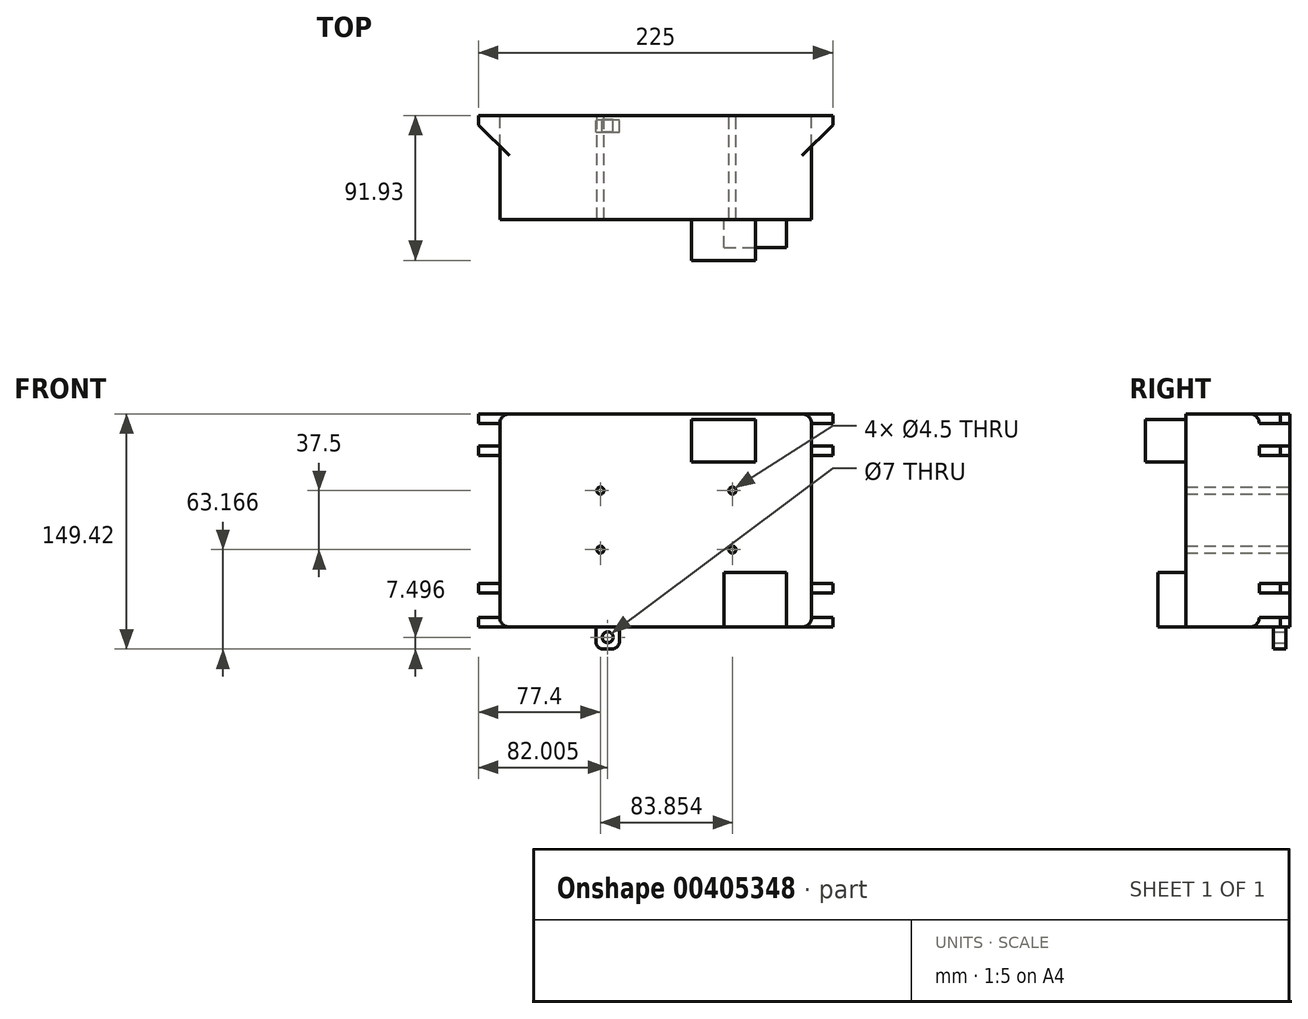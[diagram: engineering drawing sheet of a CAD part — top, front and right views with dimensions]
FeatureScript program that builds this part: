
annotation { "Feature Type Name" : "Feature", "Feature Type Description" : "" }
export const myFeature = defineFeature(function(context is Context, id is Id, definition is map)
    precondition{}
    {
        {
            var Q0;
            Q0=qCreatedBy(makeId("Front.planeOp"),FACE);
            var sketch = newSketch(context, id + "F0", { "sketchPlane" : qUnion([Q0])});
            skPoint(sketch, "E0", {"position": v(-106.19, 61.28) * mm});
            skPoint(sketch, "E1", {"position": v(91.81, -74.14) * mm});
            skPoint(sketch, "E2", {"position": v(91.81, 61.28) * mm});
            skPoint(sketch, "E3", {"position": v(-106.19, -74.14) * mm});
            skPoint(sketch, "E4", {"position": v(102.31, -60.3) * mm});
            skPoint(sketch, "E5", {"position": v(102.31, 48.09) * mm});
            skPoint(sketch, "E6", {"position": v(-116.69, 48.09) * mm});
            skPoint(sketch, "E7", {"position": v(-116.69, -60.3) * mm});
            skLineSegment(sketch, "E8.bottom", {"start": v(-100.19, 61.28) * mm, "end": v(85.81, 61.28) * mm});
            skLineSegment(sketch, "E8.top", {"start": v(-100.19, -74.14) * mm, "end": v(85.81, -74.14) * mm});
            skLineSegment(sketch, "E8.left", {"start": v(-106.19, 55.28) * mm, "end": v(-106.19, -68.14) * mm});
            skLineSegment(sketch, "E8.right", {"start": v(91.81, 55.28) * mm, "end": v(91.81, -68.14) * mm});
            skLineSegment(sketch, "E9.bottom", {"start": v(85.81, 61.28) * mm, "end": v(106.81, 61.28) * mm});
            skLineSegment(sketch, "E9.top", {"start": v(91.81, 34.9) * mm, "end": v(106.81, 34.9) * mm});
            skLineSegment(sketch, "E9.left", {"start": v(91.81, 55.28) * mm, "end": v(91.81, 34.9) * mm});
            skLineSegment(sketch, "E9.right", {"start": v(112.81, 55.28) * mm, "end": v(112.81, 40.9) * mm});
            skLineSegment(sketch, "E10.bottom", {"start": v(85.81, -74.14) * mm, "end": v(106.81, -74.14) * mm});
            skLineSegment(sketch, "E10.top", {"start": v(91.81, -46.46) * mm, "end": v(106.81, -46.46) * mm});
            skLineSegment(sketch, "E10.left", {"start": v(91.81, -68.14) * mm, "end": v(91.81, -46.46) * mm});
            skLineSegment(sketch, "E10.right", {"start": v(112.81, -68.14) * mm, "end": v(112.81, -52.46) * mm});
            skLineSegment(sketch, "E11.bottom", {"start": v(-100.19, -74.14) * mm, "end": v(-121.19, -74.14) * mm});
            skLineSegment(sketch, "E11.top", {"start": v(-106.19, -46.46) * mm, "end": v(-121.19, -46.46) * mm});
            skLineSegment(sketch, "E11.left", {"start": v(-106.19, -68.14) * mm, "end": v(-106.19, -46.46) * mm});
            skLineSegment(sketch, "E11.right", {"start": v(-127.19, -68.14) * mm, "end": v(-127.19, -52.46) * mm});
            skLineSegment(sketch, "E12.bottom", {"start": v(-106.19, 61.28) * mm, "end": v(-121.19, 61.28) * mm});
            skLineSegment(sketch, "E12.top", {"start": v(-106.19, 34.9) * mm, "end": v(-121.19, 34.9) * mm});
            skLineSegment(sketch, "E12.left", {"start": v(-106.19, 55.28) * mm, "end": v(-106.19, 34.9) * mm});
            skLineSegment(sketch, "E12.right", {"start": v(-127.19, 55.28) * mm, "end": v(-127.19, 40.9) * mm});
            skPoint(sketch, "E13.visualSharp", {"position": v(-127.19, 61.28) * mm});
            skArc(sketch, "E13.filletArc", {"start": v(-121.19, 61.28) * mm, "mid": v(-125.43, 59.52) * mm, "end": v(-127.19, 55.28) * mm});
            skPoint(sketch, "E14.visualSharp", {"position": v(-127.19, -74.14) * mm});
            skArc(sketch, "E14.filletArc", {"start": v(-127.19, -68.14) * mm, "mid": v(-125.43, -72.39) * mm, "end": v(-121.19, -74.14) * mm});
            skPoint(sketch, "E15.visualSharp", {"position": v(-127.19, -46.46) * mm});
            skArc(sketch, "E15.filletArc", {"start": v(-121.19, -46.46) * mm, "mid": v(-125.43, -48.22) * mm, "end": v(-127.19, -52.46) * mm});
            skPoint(sketch, "E16.visualSharp", {"position": v(112.81, -46.46) * mm});
            skArc(sketch, "E16.filletArc", {"start": v(112.81, -52.46) * mm, "mid": v(111.06, -48.22) * mm, "end": v(106.81, -46.46) * mm});
            skPoint(sketch, "E17.visualSharp", {"position": v(112.81, -74.14) * mm});
            skArc(sketch, "E17.filletArc", {"start": v(106.81, -74.14) * mm, "mid": v(111.06, -72.39) * mm, "end": v(112.81, -68.14) * mm});
            skPoint(sketch, "E18.visualSharp", {"position": v(112.81, 34.9) * mm});
            skArc(sketch, "E18.filletArc", {"start": v(106.81, 34.9) * mm, "mid": v(111.06, 36.66) * mm, "end": v(112.81, 40.9) * mm});
            skPoint(sketch, "E19.visualSharp", {"position": v(112.81, 61.28) * mm});
            skArc(sketch, "E19.filletArc", {"start": v(112.81, 55.28) * mm, "mid": v(111.06, 59.52) * mm, "end": v(106.81, 61.28) * mm});
            skPoint(sketch, "E20.visualSharp", {"position": v(-127.19, 34.9) * mm});
            skArc(sketch, "E20.filletArc", {"start": v(-127.19, 40.9) * mm, "mid": v(-125.43, 36.66) * mm, "end": v(-121.19, 34.9) * mm});
            skCircle(sketch, "E21", {"center": v(-116.69, -60.3) * mm, "radius": 3.75 * mm});
            skCircle(sketch, "E22", {"center": v(-116.69, 48.09) * mm, "radius": 3.75 * mm});
            skCircle(sketch, "E23", {"center": v(102.31, 48.09) * mm, "radius": 3.75 * mm});
            skCircle(sketch, "E24", {"center": v(102.31, -60.3) * mm, "radius": 3.75 * mm});
            skPoint(sketch, "E25", {"position": v(274.58, -41.3) * mm});
            skPoint(sketch, "E26", {"position": v(292.5, -41.3) * mm});
            skLineSegment(sketch, "E27.0", {"start": v(-112.19, 34.9) * mm, "end": v(-112.19, -46.46) * mm});
            skLineSegment(sketch, "E28.0", {"start": v(97.81, 34.9) * mm, "end": v(97.81, -46.46) * mm});
            skArc(sketch, "E29.filletArc", {"start": v(-100.19, 61.28) * mm, "mid": v(-104.43, 59.52) * mm, "end": v(-106.19, 55.28) * mm});
            skArc(sketch, "E30.filletArc", {"start": v(91.81, 55.28) * mm, "mid": v(90.06, 59.52) * mm, "end": v(85.81, 61.28) * mm});
            skArc(sketch, "E31.filletArc", {"start": v(85.81, -74.14) * mm, "mid": v(90.06, -72.39) * mm, "end": v(91.81, -68.14) * mm});
            skArc(sketch, "E32.filletArc", {"start": v(-106.19, -68.14) * mm, "mid": v(-104.43, -72.39) * mm, "end": v(-100.19, -74.14) * mm});
            skLineSegment(sketch, "E33", {"start": v(-106.19, 61.28) * mm, "end": v(-100.19, 61.28) * mm});
            skLineSegment(sketch, "E34.0", {"start": v(-119.69, 61.28) * mm, "end": v(-119.69, 55.28) * mm});
            skLineSegment(sketch, "E35.0", {"start": v(-106.19, 55.28) * mm, "end": v(-119.69, 55.28) * mm});
            skLineSegment(sketch, "E36.0", {"start": v(-106.19, 40.9) * mm, "end": v(-119.69, 40.9) * mm});
            skLineSegment(sketch, "E37.trimOffspring", {"start": v(-119.69, 40.9) * mm, "end": v(-119.69, 34.9) * mm});
            skLineSegment(sketch, "E38.0", {"start": v(85.81, 55.28) * mm, "end": v(105.31, 55.28) * mm});
            skLineSegment(sketch, "E39.0", {"start": v(91.81, 40.9) * mm, "end": v(105.31, 40.9) * mm});
            skLineSegment(sketch, "E40.0", {"start": v(91.81, -52.46) * mm, "end": v(105.31, -52.46) * mm});
            skLineSegment(sketch, "E41.0", {"start": v(85.81, -68.14) * mm, "end": v(105.31, -68.14) * mm});
            skLineSegment(sketch, "E42.0", {"start": v(-100.19, -68.14) * mm, "end": v(-119.69, -68.14) * mm});
            skLineSegment(sketch, "E43.0", {"start": v(-106.19, -52.46) * mm, "end": v(-119.69, -52.46) * mm});
            skLineSegment(sketch, "E44.0", {"start": v(-119.69, -74.14) * mm, "end": v(-119.69, -68.14) * mm});
            skLineSegment(sketch, "E45.0", {"start": v(105.31, 61.28) * mm, "end": v(105.31, 55.28) * mm});
            skLineSegment(sketch, "E46.trimOffspring", {"start": v(105.31, 40.9) * mm, "end": v(105.31, 34.9) * mm});
            skLineSegment(sketch, "E47.trimOffspring", {"start": v(105.31, -46.46) * mm, "end": v(105.31, -52.46) * mm});
            skLineSegment(sketch, "E48.trimOffspring", {"start": v(105.31, -68.14) * mm, "end": v(105.31, -74.14) * mm});
            skLineSegment(sketch, "E49.trimOffspring", {"start": v(-119.69, -52.46) * mm, "end": v(-119.69, -46.46) * mm});
            skLineSegment(sketch, "E50.0", {"start": v(-40.19, -88.14) * mm, "end": v(-35.19, -88.14) * mm});
            skLineSegment(sketch, "E51.0", {"start": v(-30.19, -74.14) * mm, "end": v(-30.19, -83.14) * mm});
            skLineSegment(sketch, "E52.0", {"start": v(-45.19, -74.14) * mm, "end": v(-45.19, -83.14) * mm});
            skLineSegment(sketch, "E53", {"start": v(-37.69, -88.14) * mm, "end": v(-37.69, -74.14) * mm, "construction": true});
            skLineSegment(sketch, "E54.0", {"start": v(-45.19, -80.64) * mm, "end": v(-30.19, -80.64) * mm, "construction": true});
            skCircle(sketch, "E55", {"center": v(-37.69, -80.64) * mm, "radius": 3.5 * mm});
            skPoint(sketch, "E56.visualSharp", {"position": v(-45.19, -88.14) * mm});
            skArc(sketch, "E56.filletArc", {"start": v(-45.19, -83.14) * mm, "mid": v(-43.72, -86.68) * mm, "end": v(-40.19, -88.14) * mm});
            skPoint(sketch, "E57.visualSharp", {"position": v(-30.19, -88.14) * mm});
            skArc(sketch, "E57.filletArc", {"start": v(-35.19, -88.14) * mm, "mid": v(-31.65, -86.68) * mm, "end": v(-30.19, -83.14) * mm});
            skLineSegment(sketch, "E58.0", {"start": v(-100.19, 12.53) * mm, "end": v(85.81, 12.53) * mm, "construction": true});
            skLineSegment(sketch, "E59.0", {"start": v(41.56, 55.28) * mm, "end": v(41.56, -68.14) * mm, "construction": true});
            skLineSegment(sketch, "E60.0", {"start": v(-100.19, -24.97) * mm, "end": v(85.81, -24.97) * mm, "construction": true});
            skLineSegment(sketch, "E61.0", {"start": v(-42.29, 55.28) * mm, "end": v(-42.29, -68.14) * mm, "construction": true});
            skCircle(sketch, "E62", {"center": v(-42.29, 12.53) * mm, "radius": 2.25 * mm});
            skCircle(sketch, "E63", {"center": v(41.56, 12.53) * mm, "radius": 2.25 * mm});
            skCircle(sketch, "E64", {"center": v(-42.29, -24.97) * mm, "radius": 2.25 * mm});
            skCircle(sketch, "E65", {"center": v(41.56, -24.97) * mm, "radius": 2.25 * mm});
            skSolve(sketch);
        }
        {
            var Q0;
            Q0=makeQuery(id+"F0.imprint","IMPRINT",FACE,{"disambiguationData":[TD([[makeQuery(id+"F0.imprint","IMPRINT",EDGE,{"derivedFrom":sQuery(id+"F0.wireOp",EDGE,"E8.bottom")}),-1.0]])]});
            extrude(context, id + "F1", {"entities" : qUnion([Q0]), "depth" : 66 * mm});
        }
        {
            var Q0;
            Q0=makeQuery(id+"F0.imprint","IMPRINT",FACE,{"disambiguationData":[TD([[makeQuery(id+"F0.imprint","IMPRINT",EDGE,{"derivedFrom":sQuery(id+"F0.wireOp",EDGE,"E12.right")}),1.0]])]});
            var Q1;
            Q1=makeQuery(id+"F0.imprint","IMPRINT",FACE,{"disambiguationData":[TD([[makeQuery(id+"F0.imprint","IMPRINT",EDGE,{"derivedFrom":sQuery(id+"F0.wireOp",EDGE,"E9.right")}),-1.0]])]});
            var Q2;
            Q2=makeQuery(id+"F0.imprint","IMPRINT",FACE,{"disambiguationData":[TD([[makeQuery(id+"F0.imprint","IMPRINT",EDGE,{"derivedFrom":sQuery(id+"F0.wireOp",EDGE,"E10.right")}),1.0]])]});
            var Q3;
            Q3=makeQuery(id+"F0.imprint","IMPRINT",FACE,{"disambiguationData":[TD([[makeQuery(id+"F0.imprint","IMPRINT",EDGE,{"derivedFrom":sQuery(id+"F0.wireOp",EDGE,"E11.right")}),-1.0]])]});
            var Q4;
            Q4=makeQuery(id+"F0.imprint","IMPRINT",FACE,{"disambiguationData":[TD([[makeQuery(id+"F0.imprint","IMPRINT",EDGE,{"derivedFrom":sQuery(id+"F0.wireOp",EDGE,"E29.filletArc")}),-1.0]])]});
            var Q5;
            {var subQ0=sQuery(id+"F0.wireOp",EDGE,"E36.0");Q5=makeQuery(id+"F0.imprint","IMPRINT",FACE,{"disambiguationData":[TD([[makeQuery(id+"F0.imprint","IMPRINT",EDGE,{"derivedFrom":subQ0}),1.0]])]});}
            var Q6;
            {var subQ0=sQuery(id+"F0.wireOp",EDGE,"E43.0");Q6=makeQuery(id+"F0.imprint","IMPRINT",FACE,{"disambiguationData":[TD([[makeQuery(id+"F0.imprint","IMPRINT",EDGE,{"derivedFrom":subQ0}),-1.0]])]});}
            var Q7;
            {var subQ0=sQuery(id+"F0.wireOp",EDGE,"E32.filletArc");Q7=makeQuery(id+"F0.imprint","IMPRINT",FACE,{"disambiguationData":[TD([[makeQuery(id+"F0.imprint","IMPRINT",EDGE,{"derivedFrom":subQ0}),-1.0]])]});}
            var Q8;
            {var subQ0=sQuery(id+"F0.wireOp",EDGE,"E31.filletArc");Q8=makeQuery(id+"F0.imprint","IMPRINT",FACE,{"disambiguationData":[TD([[makeQuery(id+"F0.imprint","IMPRINT",EDGE,{"derivedFrom":subQ0}),-1.0]])]});}
            var Q9;
            {var subQ0=sQuery(id+"F0.wireOp",EDGE,"E40.0");Q9=makeQuery(id+"F0.imprint","IMPRINT",FACE,{"disambiguationData":[TD([[makeQuery(id+"F0.imprint","IMPRINT",EDGE,{"derivedFrom":subQ0}),1.0]])]});}
            var Q10;
            {var subQ0=sQuery(id+"F0.wireOp",EDGE,"E39.0");Q10=makeQuery(id+"F0.imprint","IMPRINT",FACE,{"disambiguationData":[TD([[makeQuery(id+"F0.imprint","IMPRINT",EDGE,{"derivedFrom":subQ0}),-1.0]])]});}
            var Q11;
            {var subQ0=sQuery(id+"F0.wireOp",EDGE,"E30.filletArc");Q11=makeQuery(id+"F0.imprint","IMPRINT",FACE,{"disambiguationData":[TD([[makeQuery(id+"F0.imprint","IMPRINT",EDGE,{"derivedFrom":subQ0}),-1.0]])]});}
            extrude(context, id + "F2", {"entities" : qUnion([Q0, Q1, Q2, Q3, Q4, Q5, Q6, Q7, Q8, Q9, Q10, Q11]), "operationType" : NewBodyOperationType.ADD, "depth" : 6 * mm});
        }
        {
            var Q0;
            Q0=makeQuery(id+"F7.boolean.opBoolean","MERGE",FACE,{"derivedFrom":[makeQuery(id+"F2.boolean.opBoolean","MERGE",FACE,{"derivedFrom":[makeQuery(id+"F1.opExtrude","SWEPT_FACE",FACE,{"disambiguationData":[OSD([sQuery(id+"F0.wireOp",EDGE,"E8.top")])]}),makeQuery(id+"F2.opExtrude","SWEPT_FACE",FACE,{"disambiguationData":[OSD([sQuery(id+"F0.wireOp",EDGE,"E10.bottom")])]}),makeQuery(id+"F2.opExtrude","SWEPT_FACE",FACE,{"disambiguationData":[OSD([sQuery(id+"F0.wireOp",EDGE,"E11.bottom")])]})]}),makeQuery(id+"F7.opExtrude","SWEPT_FACE",FACE,{"disambiguationData":[OSD([sQuery(id+"F5.wireOp",EDGE,"E81.top")])]})]});
            var sketch = newSketch(context, id + "F3", { "sketchPlane" : qUnion([Q0])});
            skPoint(sketch, "E66.0", {"position": v(-119.69, 0) * mm});
            skLineSegment(sketch, "E67", {"start": v(-119.69, 0) * mm, "end": v(-119.69, 6) * mm, "construction": true});
            skLineSegment(sketch, "E68", {"start": v(-119.69, 6) * mm, "end": v(-100.19, 25.5) * mm});
            skPoint(sketch, "E69.0", {"position": v(105.31, 0) * mm});
            skLineSegment(sketch, "E70", {"start": v(105.31, 0) * mm, "end": v(105.31, 6) * mm, "construction": true});
            skLineSegment(sketch, "E71", {"start": v(105.31, 6) * mm, "end": v(85.81, 25.5) * mm});
            skSolve(sketch);
        }
        {
            var Q0;
            Q0=sQuery(id+"F3.wireOp",EDGE,"E68");
            var Q1;
            Q1=sQuery(id+"F3.wireOp",EDGE,"E71");
            extrude(context, id + "F4", {"bodyType" : ExtendedToolBodyType.SURFACE, "surfaceEntities" : qUnion([Q0, Q1]), "oppositeDirection" : true, "depth" : 140 * mm});
        }
        {
            var Q0;
            Q0=makeQuery(id+"F1.opExtrude","CAP_FACE",FACE,{"disambiguationData":[OSD([sQuery(id+"F0.wireOp",EDGE,"E8.bottom"),sQuery(id+"F0.wireOp",EDGE,"E8.top"),sQuery(id+"F0.wireOp",EDGE,"E8.left"),sQuery(id+"F0.wireOp",EDGE,"E8.right"),sQuery(id+"F0.wireOp",EDGE,"E9.left"),sQuery(id+"F0.wireOp",EDGE,"E10.left"),sQuery(id+"F0.wireOp",EDGE,"E11.left"),sQuery(id+"F0.wireOp",EDGE,"E12.left")])],"isStart":false});
            var sketch = newSketch(context, id + "F5", { "sketchPlane" : qUnion([Q0])});
            skLineSegment(sketch, "E72.bottom", {"start": v(56.3, 30.69) * mm, "end": v(15.42, 30.69) * mm});
            skLineSegment(sketch, "E72.top", {"start": v(56.3, 57.71) * mm, "end": v(15.42, 57.71) * mm});
            skLineSegment(sketch, "E72.left", {"start": v(56.3, 30.69) * mm, "end": v(56.3, 57.71) * mm});
            skLineSegment(sketch, "E72.right", {"start": v(15.42, 30.69) * mm, "end": v(15.42, 57.71) * mm});
            skLineSegment(sketch, "E73.bottom", {"start": v(39.39, 23.56) * mm, "end": v(43.09, 23.56) * mm});
            skLineSegment(sketch, "E73.top", {"start": v(39.39, 7.16) * mm, "end": v(43.09, 7.16) * mm});
            skLineSegment(sketch, "E73.left", {"start": v(33.04, 17.21) * mm, "end": v(33.04, 13.51) * mm});
            skLineSegment(sketch, "E73.right", {"start": v(49.44, 17.21) * mm, "end": v(49.44, 13.51) * mm});
            skCircle(sketch, "E74", {"center": v(77.27, 25.31) * mm, "radius": 3.63 * mm});
            skCircle(sketch, "E75", {"center": v(75.52, 52.06) * mm, "radius": 5.1 * mm});
            skLineSegment(sketch, "E76.bottom", {"start": v(-55.7, 38.34) * mm, "end": v(-106.19, 38.34) * mm});
            skLineSegment(sketch, "E76.top", {"start": v(-55.7, -49.16) * mm, "end": v(-106.19, -49.16) * mm});
            skLineSegment(sketch, "E76.left", {"start": v(-55.7, 38.34) * mm, "end": v(-55.7, -49.16) * mm});
            skLineSegment(sketch, "E76.right", {"start": v(-106.19, 38.34) * mm, "end": v(-106.19, -49.16) * mm});
            skLineSegment(sketch, "E77.bottom", {"start": v(-39.8, -34.58) * mm, "end": v(-55.7, -34.58) * mm});
            skLineSegment(sketch, "E77.top", {"start": v(-46.14, -19.32) * mm, "end": v(-55.7, -19.32) * mm});
            skLineSegment(sketch, "E77.left", {"start": v(-39.8, -34.58) * mm, "end": v(-39.8, -25.67) * mm});
            skLineSegment(sketch, "E77.right", {"start": v(-55.7, -34.58) * mm, "end": v(-55.7, -19.32) * mm});
            skLineSegment(sketch, "E78.bottom", {"start": v(-39.61, 23.57) * mm, "end": v(-55.7, 23.57) * mm});
            skLineSegment(sketch, "E78.top", {"start": v(-45.96, 7.95) * mm, "end": v(-55.7, 7.95) * mm});
            skLineSegment(sketch, "E78.left", {"start": v(-39.61, 23.57) * mm, "end": v(-39.61, 14.3) * mm});
            skLineSegment(sketch, "E78.right", {"start": v(-55.7, 23.57) * mm, "end": v(-55.7, 7.95) * mm});
            skCircle(sketch, "E79", {"center": v(4.35, -58.27) * mm, "radius": 15.26 * mm});
            skLineSegment(sketch, "E80.bottom", {"start": v(39.24, -18.96) * mm, "end": v(43.4, -18.96) * mm});
            skLineSegment(sketch, "E80.top", {"start": v(39.24, -35.83) * mm, "end": v(43.4, -35.83) * mm});
            skLineSegment(sketch, "E80.left", {"start": v(32.89, -25.31) * mm, "end": v(32.89, -29.48) * mm});
            skLineSegment(sketch, "E80.right", {"start": v(49.76, -25.31) * mm, "end": v(49.76, -29.48) * mm});
            skLineSegment(sketch, "E81.bottom", {"start": v(36.3, -39.43) * mm, "end": v(75.96, -39.43) * mm});
            skLineSegment(sketch, "E81.top", {"start": v(36.3, -74.14) * mm, "end": v(75.96, -74.14) * mm});
            skLineSegment(sketch, "E81.left", {"start": v(36.3, -39.43) * mm, "end": v(36.3, -74.14) * mm});
            skLineSegment(sketch, "E81.right", {"start": v(75.96, -39.43) * mm, "end": v(75.96, -74.14) * mm});
            skCircle(sketch, "E82", {"center": v(84.03, -38.88) * mm, "radius": 3.41 * mm});
            skPoint(sketch, "E83.visualSharp", {"position": v(-39.61, 7.95) * mm});
            skArc(sketch, "E83.filletArc", {"start": v(-45.96, 7.95) * mm, "mid": v(-41.47, 9.81) * mm, "end": v(-39.61, 14.3) * mm});
            skPoint(sketch, "E84.visualSharp", {"position": v(-39.8, -19.32) * mm});
            skArc(sketch, "E84.filletArc", {"start": v(-39.8, -25.67) * mm, "mid": v(-41.65, -21.18) * mm, "end": v(-46.14, -19.32) * mm});
            skPoint(sketch, "E85.visualSharp", {"position": v(32.89, -18.96) * mm});
            skArc(sketch, "E85.filletArc", {"start": v(39.24, -18.96) * mm, "mid": v(34.75, -20.82) * mm, "end": v(32.89, -25.31) * mm});
            skPoint(sketch, "E86.visualSharp", {"position": v(32.89, -35.83) * mm});
            skArc(sketch, "E86.filletArc", {"start": v(32.89, -29.48) * mm, "mid": v(34.75, -33.97) * mm, "end": v(39.24, -35.83) * mm});
            skPoint(sketch, "E87.visualSharp", {"position": v(49.76, -35.83) * mm});
            skArc(sketch, "E87.filletArc", {"start": v(43.4, -35.83) * mm, "mid": v(47.9, -33.97) * mm, "end": v(49.76, -29.48) * mm});
            skPoint(sketch, "E88.visualSharp", {"position": v(49.76, -18.96) * mm});
            skArc(sketch, "E88.filletArc", {"start": v(49.76, -25.31) * mm, "mid": v(47.9, -20.82) * mm, "end": v(43.4, -18.96) * mm});
            skPoint(sketch, "E89.visualSharp", {"position": v(49.44, 7.16) * mm});
            skArc(sketch, "E89.filletArc", {"start": v(43.09, 7.16) * mm, "mid": v(47.58, 9.02) * mm, "end": v(49.44, 13.51) * mm});
            skPoint(sketch, "E90.visualSharp", {"position": v(33.04, 7.16) * mm});
            skArc(sketch, "E90.filletArc", {"start": v(33.04, 13.51) * mm, "mid": v(34.9, 9.02) * mm, "end": v(39.39, 7.16) * mm});
            skPoint(sketch, "E91.visualSharp", {"position": v(33.04, 23.56) * mm});
            skArc(sketch, "E91.filletArc", {"start": v(39.39, 23.56) * mm, "mid": v(34.9, 21.7) * mm, "end": v(33.04, 17.21) * mm});
            skPoint(sketch, "E92.visualSharp", {"position": v(49.44, 23.56) * mm});
            skArc(sketch, "E92.filletArc", {"start": v(49.44, 17.21) * mm, "mid": v(47.58, 21.7) * mm, "end": v(43.09, 23.56) * mm});
            skSolve(sketch);
        }
        {
            var Q0;
            Q0=makeQuery(id+"F5.imprint","IMPRINT",FACE,{"disambiguationData":[TD([[makeQuery(id+"F5.imprint","IMPRINT",EDGE,{"derivedFrom":sQuery(id+"F5.wireOp",EDGE,"E72.bottom")}),-1.0]])]});
            extrude(context, id + "F6", {"entities" : qUnion([Q0]), "operationType" : NewBodyOperationType.ADD, "depth" : 91.93 * mm - 66 * mm});
        }
        {
            var Q0;
            Q0=makeQuery(id+"F5.imprint","IMPRINT",FACE,{"disambiguationData":[TD([[makeQuery(id+"F5.imprint","IMPRINT",EDGE,{"derivedFrom":sQuery(id+"F5.wireOp",EDGE,"E81.bottom")}),-1.0]])]});
            extrude(context, id + "F7", {"entities" : qUnion([Q0]), "operationType" : NewBodyOperationType.ADD, "depth" : 17.93 * mm});
        }
        {
            var Q0;
            Q0=makeQuery(id+"F0.imprint","IMPRINT",FACE,{"disambiguationData":[TD([[makeQuery(id+"F0.imprint","IMPRINT",EDGE,{"derivedFrom":sQuery(id+"F0.wireOp",EDGE,"E29.filletArc")}),-1.0]])]});
            var Q1;
            {var subQ0=sQuery(id+"F0.wireOp",EDGE,"E36.0");Q1=makeQuery(id+"F0.imprint","IMPRINT",FACE,{"disambiguationData":[TD([[makeQuery(id+"F0.imprint","IMPRINT",EDGE,{"derivedFrom":subQ0}),1.0]])]});}
            var Q2;
            {var subQ0=sQuery(id+"F0.wireOp",EDGE,"E43.0");Q2=makeQuery(id+"F0.imprint","IMPRINT",FACE,{"disambiguationData":[TD([[makeQuery(id+"F0.imprint","IMPRINT",EDGE,{"derivedFrom":subQ0}),-1.0]])]});}
            var Q3;
            {var subQ0=sQuery(id+"F0.wireOp",EDGE,"E32.filletArc");Q3=makeQuery(id+"F0.imprint","IMPRINT",FACE,{"disambiguationData":[TD([[makeQuery(id+"F0.imprint","IMPRINT",EDGE,{"derivedFrom":subQ0}),-1.0]])]});}
            var Q4;
            Q4=makeQuery(id+"F4.opExtrude","SWEPT_FACE",FACE,{"disambiguationData":[OSD([sQuery(id+"F3.wireOp",EDGE,"E68")])]});
            extrude(context, id + "F8", {"entities" : qUnion([Q0, Q1, Q2, Q3]), "operationType" : NewBodyOperationType.ADD, "endBound" : BoundingType.UP_TO_SURFACE, "endBoundEntityFace" : qUnion([Q4]), "depth" : 25.4 * mm});
        }
        {
            var Q0;
            {var subQ0=sQuery(id+"F0.wireOp",EDGE,"E30.filletArc");Q0=makeQuery(id+"F0.imprint","IMPRINT",FACE,{"disambiguationData":[TD([[makeQuery(id+"F0.imprint","IMPRINT",EDGE,{"derivedFrom":subQ0}),-1.0]])]});}
            var Q1;
            {var subQ0=sQuery(id+"F0.wireOp",EDGE,"E39.0");Q1=makeQuery(id+"F0.imprint","IMPRINT",FACE,{"disambiguationData":[TD([[makeQuery(id+"F0.imprint","IMPRINT",EDGE,{"derivedFrom":subQ0}),-1.0]])]});}
            var Q2;
            {var subQ0=sQuery(id+"F0.wireOp",EDGE,"E40.0");Q2=makeQuery(id+"F0.imprint","IMPRINT",FACE,{"disambiguationData":[TD([[makeQuery(id+"F0.imprint","IMPRINT",EDGE,{"derivedFrom":subQ0}),1.0]])]});}
            var Q3;
            {var subQ0=sQuery(id+"F0.wireOp",EDGE,"E31.filletArc");Q3=makeQuery(id+"F0.imprint","IMPRINT",FACE,{"disambiguationData":[TD([[makeQuery(id+"F0.imprint","IMPRINT",EDGE,{"derivedFrom":subQ0}),-1.0]])]});}
            var Q4;
            Q4=makeQuery(id+"F4.opExtrude","SWEPT_FACE",FACE,{"disambiguationData":[OSD([sQuery(id+"F3.wireOp",EDGE,"E71")])]});
            extrude(context, id + "F9", {"entities" : qUnion([Q0, Q1, Q2, Q3]), "operationType" : NewBodyOperationType.ADD, "endBound" : BoundingType.UP_TO_SURFACE, "endBoundEntityFace" : qUnion([Q4]), "depth" : 25.4 * mm});
        }
        {
            var Q0;
            Q0=makeQuery(id+"F0.imprint","IMPRINT",FACE,{"disambiguationData":[TD([[makeQuery(id+"F0.imprint","IMPRINT",EDGE,{"derivedFrom":sQuery(id+"F0.wireOp",EDGE,"E50.0")}),1.0]])]});
            extrude(context, id + "F10", {"entities" : qUnion([Q0]), "operationType" : NewBodyOperationType.ADD, "depth" : 10.5 * mm, "hasSecondDirection" : true, "secondDirectionOppositeDirection" : false, "secondDirectionDepth" : 2.5 * mm});
        }
    });
